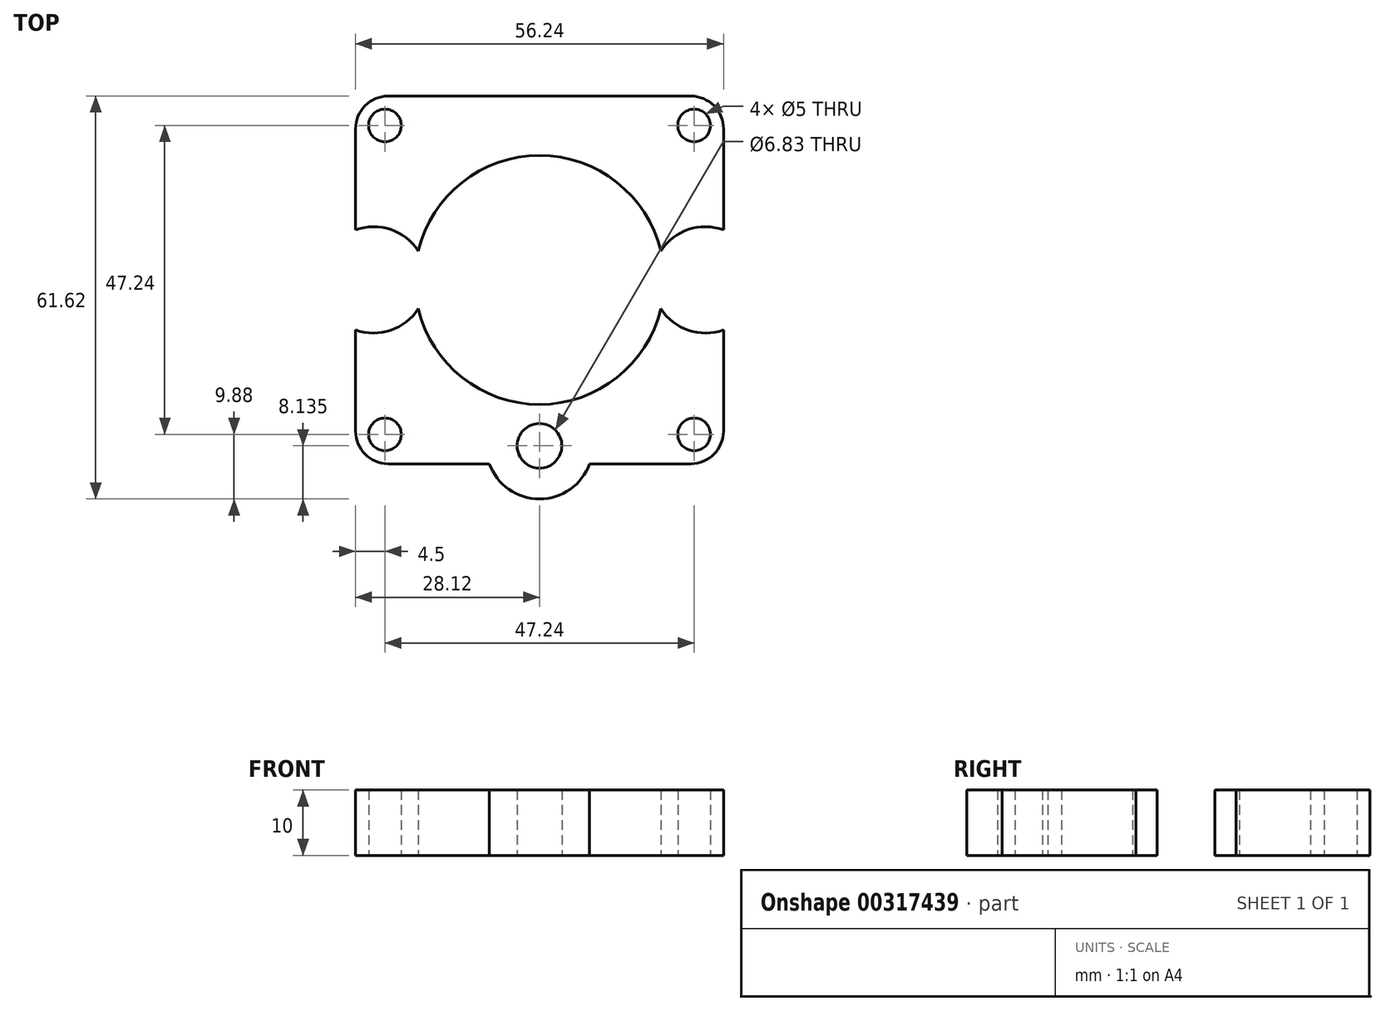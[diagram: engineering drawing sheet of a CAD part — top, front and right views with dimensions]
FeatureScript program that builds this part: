
annotation { "Feature Type Name" : "Feature", "Feature Type Description" : "" }
export const myFeature = defineFeature(function(context is Context, id is Id, definition is map)
    precondition{}
    {
        {
            var Q0;
            Q0=qCreatedBy(makeId("Top.planeOp"),FACE);
            var sketch = newSketch(context, id + "F0", { "sketchPlane" : qUnion([Q0])});
            skLineSegment(sketch, "E0.rect.bottom", {"start": v(-28.11, 28.11) * mm, "end": v(28.12, 28.11) * mm});
            skLineSegment(sketch, "E0.rect.top", {"start": v(-28.11, -28.11) * mm, "end": v(28.11, -28.11) * mm});
            skLineSegment(sketch, "E0.rect.left", {"start": v(-28.11, 28.12) * mm, "end": v(-28.12, -28.11) * mm});
            skLineSegment(sketch, "E0.rect.right", {"start": v(28.12, 28.12) * mm, "end": v(28.11, -28.11) * mm});
            skPoint(sketch, "E0.rect.middle", {"position": v(0, 0) * mm});
            skCircle(sketch, "E1", {"center": v(0, 0) * mm, "radius": 19.04 * mm});
            skCircle(sketch, "E2", {"center": v(0, 0) * mm, "radius": 3.98 * mm});
            skCircle(sketch, "E3", {"center": v(-23.62, 23.62) * mm, "radius": 2.5 * mm});
            skCircle(sketch, "E4", {"center": v(23.62, 23.62) * mm, "radius": 2.5 * mm});
            skCircle(sketch, "E5", {"center": v(23.62, -23.62) * mm, "radius": 2.5 * mm});
            skCircle(sketch, "E6", {"center": v(-23.62, -23.62) * mm, "radius": 2.5 * mm});
            skLineSegment(sketch, "E7.rect.bottom", {"start": v(-23.62, 23.62) * mm, "end": v(23.62, 23.62) * mm, "construction": true});
            skLineSegment(sketch, "E7.rect.top", {"start": v(-23.62, -23.62) * mm, "end": v(23.62, -23.62) * mm, "construction": true});
            skLineSegment(sketch, "E7.rect.left", {"start": v(-23.62, 23.62) * mm, "end": v(-23.62, -23.62) * mm, "construction": true});
            skLineSegment(sketch, "E7.rect.right", {"start": v(23.62, 23.62) * mm, "end": v(23.62, -23.62) * mm, "construction": true});
            skCircle(sketch, "E8", {"center": v(0, 0) * mm, "radius": 5.38 * mm});
            skCircle(sketch, "E9", {"center": v(-25.37, 0) * mm, "radius": 8.13 * mm});
            skCircle(sketch, "E10", {"center": v(25.37, 0) * mm, "radius": 8.13 * mm});
            skCircle(sketch, "E11", {"center": v(0, -25.37) * mm, "radius": 8.13 * mm});
            skCircle(sketch, "E12", {"center": v(-25.37, 0) * mm, "radius": 3.42 * mm});
            skCircle(sketch, "E13", {"center": v(25.37, 0) * mm, "radius": 3.41 * mm});
            skCircle(sketch, "E14", {"center": v(0, -25.37) * mm, "radius": 3.42 * mm});
            skSolve(sketch);
        }
        {
            var Q0;
            {var subQ6=sQuery(id+"F0.wireOp",EDGE,"E0.rect.bottom");Q0=makeQuery(id+"F0.imprint","IMPRINT",FACE,{"disambiguationData":[TD([[makeQuery(id+"F0.imprint","IMPRINT",EDGE,{"derivedFrom":subQ6}),-1.0]])]});}
            var Q1;
            {var subQ0=sQuery(id+"F0.wireOp",EDGE,"E9");var subQ1=sQuery(id+"F0.wireOp",EDGE,"E0.rect.left");var subQ2=makeQuery(id+"F0.imprint","INTERSECT",VERTEX,{"disambiguationData":[OD(0.0)],"derivedFrom":[subQ1,subQ0]});Q1=makeQuery(id+"F0.imprint","IMPRINT",FACE,{"disambiguationData":[TD([[makeQuery(id+"F0.imprint","IMPRINT",EDGE,{"disambiguationData":[TD([[subQ2,-1.0]])],"derivedFrom":subQ1}),-1.0]])]});}
            var Q2;
            {var subQ0=sQuery(id+"F0.wireOp",EDGE,"E9");var subQ1=sQuery(id+"F0.wireOp",EDGE,"E0.rect.left");var subQ2=makeQuery(id+"F0.imprint","INTERSECT",VERTEX,{"disambiguationData":[OD(0.0)],"derivedFrom":[subQ1,subQ0]});Q2=makeQuery(id+"F0.imprint","IMPRINT",FACE,{"disambiguationData":[TD([[makeQuery(id+"F0.imprint","IMPRINT",EDGE,{"disambiguationData":[TD([[subQ2,-1.0]])],"derivedFrom":subQ1}),1.0]])]});}
            var Q3;
            Q3=makeQuery(id+"F0.imprint","IMPRINT",FACE,{"disambiguationData":[TD([[makeQuery(id+"F0.imprint","IMPRINT",EDGE,{"derivedFrom":sQuery(id+"F0.wireOp",EDGE,"E6")}),-1.0]])]});
            var Q4;
            {var subQ0=sQuery(id+"F0.wireOp",EDGE,"E10");var subQ1=sQuery(id+"F0.wireOp",EDGE,"E0.rect.right");var subQ2=makeQuery(id+"F0.imprint","INTERSECT",VERTEX,{"disambiguationData":[OD(0.0)],"derivedFrom":[subQ1,subQ0]});Q4=makeQuery(id+"F0.imprint","IMPRINT",FACE,{"disambiguationData":[TD([[makeQuery(id+"F0.imprint","IMPRINT",EDGE,{"disambiguationData":[TD([[subQ2,-1.0]])],"derivedFrom":subQ1}),-1.0]])]});}
            var Q5;
            {var subQ0=sQuery(id+"F0.wireOp",EDGE,"E10");var subQ1=sQuery(id+"F0.wireOp",EDGE,"E0.rect.right");var subQ2=makeQuery(id+"F0.imprint","INTERSECT",VERTEX,{"disambiguationData":[OD(0.0)],"derivedFrom":[subQ1,subQ0]});Q5=makeQuery(id+"F0.imprint","IMPRINT",FACE,{"disambiguationData":[TD([[makeQuery(id+"F0.imprint","IMPRINT",EDGE,{"disambiguationData":[TD([[subQ2,-1.0]])],"derivedFrom":subQ1}),1.0]])]});}
            var Q6;
            Q6=makeQuery(id+"F0.imprint","IMPRINT",FACE,{"disambiguationData":[TD([[makeQuery(id+"F0.imprint","IMPRINT",EDGE,{"derivedFrom":sQuery(id+"F0.wireOp",EDGE,"E5")}),-1.0]])]});
            var Q7;
            {var subQ0=sQuery(id+"F0.wireOp",EDGE,"E11");var subQ1=sQuery(id+"F0.wireOp",EDGE,"E0.rect.top");var subQ2=makeQuery(id+"F0.imprint","INTERSECT",VERTEX,{"disambiguationData":[OD(0.0)],"derivedFrom":[subQ1,subQ0]});Q7=makeQuery(id+"F0.imprint","IMPRINT",FACE,{"disambiguationData":[TD([[makeQuery(id+"F0.imprint","IMPRINT",EDGE,{"disambiguationData":[TD([[subQ2,-1.0]])],"derivedFrom":subQ1}),1.0]])]});}
            var Q8;
            {var subQ0=sQuery(id+"F0.wireOp",EDGE,"E11");var subQ1=sQuery(id+"F0.wireOp",EDGE,"E0.rect.top");var subQ2=makeQuery(id+"F0.imprint","INTERSECT",VERTEX,{"disambiguationData":[OD(0.0)],"derivedFrom":[subQ1,subQ0]});Q8=makeQuery(id+"F0.imprint","IMPRINT",FACE,{"disambiguationData":[TD([[makeQuery(id+"F0.imprint","IMPRINT",EDGE,{"disambiguationData":[TD([[subQ2,-1.0]])],"derivedFrom":subQ1}),-1.0]])]});}
            extrude(context, id + "F1", {"entities" : qUnion([Q0, Q1, Q2, Q3, Q4, Q5, Q6, Q7, Q8]), "depth" : 35 * mm, "hasSecondDirection" : true, "secondDirectionOppositeDirection" : false, "secondDirectionDepth" : 25 * mm});
        }
        {
            var Q0;
            Q0=makeQuery(id+"F1.opExtrude","SWEPT_EDGE",EDGE,{"disambiguationData":[OSD([sQuery(id+"F0.wireOp",EDGE,"E0.rect.top"),sQuery(id+"F0.wireOp",EDGE,"E0.rect.left")])]});
            var Q1;
            Q1=makeQuery(id+"F1.opExtrude","SWEPT_EDGE",EDGE,{"disambiguationData":[OSD([sQuery(id+"F0.wireOp",EDGE,"E0.rect.top"),sQuery(id+"F0.wireOp",EDGE,"E0.rect.right")])]});
            var Q2;
            Q2=makeQuery(id+"F1.opExtrude","SWEPT_EDGE",EDGE,{"disambiguationData":[OSD([sQuery(id+"F0.wireOp",EDGE,"E0.rect.bottom"),sQuery(id+"F0.wireOp",EDGE,"E0.rect.right")])]});
            var Q3;
            Q3=makeQuery(id+"F1.opExtrude","SWEPT_EDGE",EDGE,{"disambiguationData":[OSD([sQuery(id+"F0.wireOp",EDGE,"E0.rect.bottom"),sQuery(id+"F0.wireOp",EDGE,"E0.rect.left")])]});
            fillet(context, id + "F2", {"entities" : qUnion([Q0, Q1, Q2, Q3]), "radius" : 5 * mm, "tangentPropagation" : true, "allowEdgeOverflow" : false});
        }
    });
